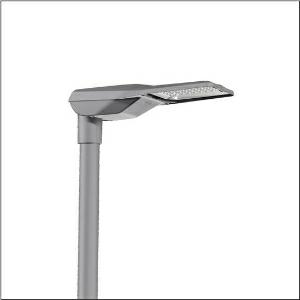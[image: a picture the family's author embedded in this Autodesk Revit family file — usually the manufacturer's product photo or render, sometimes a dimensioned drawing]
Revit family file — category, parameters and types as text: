
# Revit family: streetlight_sl_21_iq_mini___st1_0a_5xe2d61g08hb_24ab
name_source: partatom
category: Lighting Fixtures
units: mm (PartAtom-declared; Revit-internal decimal feet)

## family parameters
Cut with Voids When Loaded = No
Host = Face
Light Source = No
Part Type = Normal
Room Calculation Point = No
Round Connector Dimension = Use Diameter
Shared = No

## types (1)
- --- (1 x LED, 8480 lm, 70.9 W, 2700K)
    Apparent Load = 71 VA
    CIE Flux Codes = 37 72 97 100 100
    Color Rendering = 70
    Color Temperature = 2700K
    Default Elevation = 1800 mm
    Description = Streetlight SL 21 iQ mini, mast luminaire, primary light control with lens, of PMMA, primary optical cover: cover, of toughened safety glass, transparent, light distribution: ST1.0a, light emission: direct distribution, primary light characteristic: asymmetric, installation type: post-top, side-entry, LED, High Power LED, rated luminous flux: 8.480lm, luminous efficacy: 120lm/W, light colour: 727, colour temperature: 2700K, control gear: iQ Street-Remote, control: Street-Remote, Auto-Match, Temp-Guard, Lumen-Switch, Night-Set, Smart-Wire, Light-Fading, Desk-Remote (wireless, voltage-free reading and setting of iQ features in the workshop via application-optimized NFC function/RFID function), optimised constant luminous flux control (CLO 2.0), pre-setting: linear dimming characteristic, mains connection: 220..240V, AC, 50/60Hz, start of lifetime: 71W, end of service life: 75W, reduction: 31W, luminaire housing, of diecast aluminium, powder-coated, SITECO metallic grey (DB 702S), corrosivity category C5 high according to DIN EN ISO 12944, please order mast flange separately, inclination adjustable: 0°, 5°, 10°, 15°, sealing non-destructively replaceable, multi-level sealing system, length: 628mm, width: 235mm, height: 110mm, mast flange for spigot size: 42mm (side-entry): 5XC10008XM4, 60/48mm (side-entry/post-top): 5XC10108XM2, 76/60mm (side-entry/post-top): 5XC10108XM1, mounting height: 4..8m, protection rating (complete): IP66, insulation class (complete): insulation class II (safety insulation), certification: CE, ENEC, ENEC+, VDE, impact resistance: IK10, permissible operating ambient temperature for outdoor applications: -40..+50°C, standard-compliant lighting for roads and squares, packaging unit: 1 piece

Light Distribution: ST1.0a
    Height = 110 mm
    Lamp = 1 x LED
    Lamp Light Flux = 8480 lm
    Lamp Power = 70.9 W
    Lamp count = 1
    Length = 625 mm
    Luminous efficacy = 120 lm/W
    Manufacturer = Siteco
    ModVariant = No
    Model = 5XE2D61G08HB
    Number of Poles = 1
    OnlyDefault = Yes
    Power Factor = 1
    Product Name = Streetlight SL 21 iQ mini | ST1.0a
    Product group = mast luminaire | pylon top
    ProductGroupID = 6100
    Protection Class = Protection class II
    Protection Degree = IP 66
    RLX_Detail_Level = 1
    RLX_Emergency_Light_Flux = 0 lm
    RLX_Emergency_Type = 0
    RLX_Emergency_Type_DB = No
    RlxData = <blob elided: 26277 chars, md5=fa59271b>
    Socket = socket
    Standby Power = 0 W
    System Light Flux = 8480 lm
    System Power = 71 W
    Type Comments = factory setting: luminous flux: 100 % | dim-lin: 254 | 711 mA
    Type Image = l_1003519.jpg
    URL = http://relux.com
    VarID = @adj_157679
    Voltage = 0 V
    Weight = 0.00 kg
    Width = 234 mm

## geometry (parser evidence)
native form markers: Blend x4, Sweep x12
no freeform markers — native parametric forms only
